# Revit family: Help
name_source: partatom
category: Mass
revit_build: Autodesk Revit Architecture 2012 (Build: 20110309_2315(x64)
units: mm (PartAtom-declared; Revit-internal decimal feet)

## types (1)
- Help
    1 = 52.0015680625 "
    10 = 19.656948390625 "
    11 = 33.969858125 "
    12 = 6.500196007812 "
    13 = 46.037645171875 "
    14 = 60.179038445312 "
    15 = 26.67573540625 "
    16 = 59.588203 "
    17 = 7.975567265625 "
    18 = 12.2489791875 "
    19 = 75.744772875 "
    2 = 54.126705007812 "
    20 = 27.08895121875 "
    21 = 23.815387125 "
    22 = 51.520041421875 "
    23 = 44.8923496875 "
    24 = 9.38162203125 "
    25 = 25.448597015625 "
    26 = 9.645843265625 "
    27 = 16.79800390625 "
    28 = 63.138518351563 "
    29 = 20.078035195313 "
    3 = 106.159595664063 "
    30 = 63.22617109375 "
    4 = 54.49577428125 "
    5 = 47.99626734375 "
    6 = 95.898681140625 "
    7 = 40.313693765625 "
    8 = 83.377460742188 "
    9 = 12.53034140625 "
    Default Elevation = 48 "
    L = 252.60156 "
    W = 198.42188 "

## geometry (parser evidence)
native form markers: Blend x8, Sweep x2
no freeform markers — native parametric forms only
